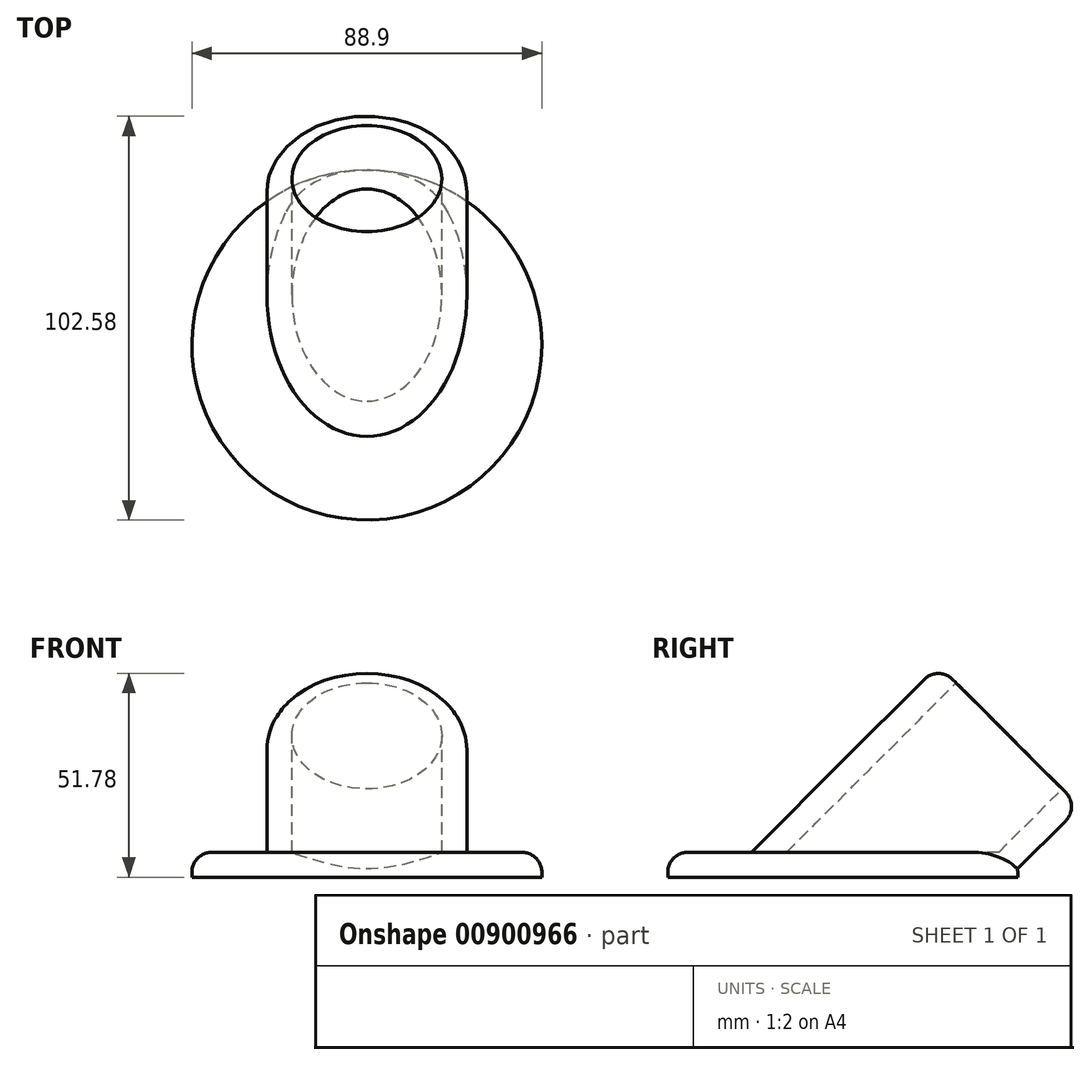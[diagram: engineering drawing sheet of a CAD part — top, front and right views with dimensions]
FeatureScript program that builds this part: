
annotation { "Feature Type Name" : "Feature", "Feature Type Description" : "" }
export const myFeature = defineFeature(function(context is Context, id is Id, definition is map)
    precondition{}
    {
        {
            var Q0;
            Q0=qCreatedBy(makeId("Top.planeOp"),FACE);
            var sketch = newSketch(context, id + "F0", { "sketchPlane" : qUnion([Q0])});
            skCircle(sketch, "E0", {"center": v(0, 0) * mm, "radius": 44.45 * mm});
            skSolve(sketch);
        }
        {
            var Q0;
            Q0=makeQuery(id+"F0.imprint","IMPRINT",FACE,{"disambiguationData":[TD([[makeQuery(id+"F0.imprint","IMPRINT",EDGE,{"derivedFrom":sQuery(id+"F0.wireOp",EDGE,"E0")}),1.0]])]});
            extrude(context, id + "F1", {"entities" : qUnion([Q0]), "depth" : 6.35 * mm, "offsetDistance" : 25.4 * mm});
        }
        {
            var Q0;
            Q0=qCreatedBy(makeId("Right.planeOp"),FACE);
            var sketch = newSketch(context, id + "F2", { "sketchPlane" : qUnion([Q0])});
            skLineSegment(sketch, "E1", {"start": v(0, 0) * mm, "end": v(0, 6.35) * mm});
            skLineSegment(sketch, "E2", {"start": v(0, 6.35) * mm, "end": v(35.92, 42.27) * mm});
            skSolve(sketch);
        }
        {
            var Q0;
            Q0=sQuery(id+"F2.wireOp",EDGE,"E2");
            var Q1;
            Q1=sQuery(id+"F2.wireOp",VERTEX,"E2.end");
            cPlane(context, id + "F3", {"entities" : qUnion([Q0, Q1]), "cplaneType" : CPlaneType.LINE_POINT, "offset" : 25.4 * mm, "width" : 152.4 * mm, "height" : 152.4 * mm});
        }
        {
            var Q0;
            Q0=qCreatedBy(id+"F3.planeOp",FACE);
            var sketch = newSketch(context, id + "F4", { "sketchPlane" : qUnion([Q0])});
            skPoint(sketch, "E3.0", {"position": v(0, -4.5) * mm});
            skCircle(sketch, "E4", {"center": v(0, -4.5) * mm, "radius": 19.05 * mm});
            skCircle(sketch, "E5", {"center": v(0, -4.5) * mm, "radius": 25.4 * mm});
            skSolve(sketch);
        }
        {
            var Q0;
            Q0=makeQuery(id+"F4.imprint","IMPRINT",FACE,{"disambiguationData":[TD([[makeQuery(id+"F4.imprint","IMPRINT",EDGE,{"derivedFrom":sQuery(id+"F4.wireOp",EDGE,"E4")}),-1.0]])]});
            var Q1;
            Q1=makeQuery(id+"F1.opExtrude","CAP_FACE",FACE,{"disambiguationData":[OSD([sQuery(id+"F0.wireOp",EDGE,"E0")])],"isStart":false});
            extrude(context, id + "F5", {"entities" : qUnion([Q0]), "operationType" : NewBodyOperationType.ADD, "endBound" : BoundingType.UP_TO_SURFACE, "oppositeDirection" : true, "depth" : 25.4 * mm, "endBoundEntityFace" : qUnion([Q1]), "offsetDistance" : 25.4 * mm});
        }
        {
            var Q0;
            Q0=makeQuery(id+"F5.opExtrude","CAP_EDGE",EDGE,{"disambiguationData":[OSD([sQuery(id+"F4.wireOp",EDGE,"E5")])],"isStart":false});
            fillet(context, id + "F6", {"entities" : qUnion([Q0]), "radius" : 12.7 * mm, "tangentPropagation" : true, "allowEdgeOverflow" : false});
        }
        {
            var Q0;
            Q0=makeQuery(id+"F1.opExtrude","CAP_EDGE",EDGE,{"disambiguationData":[OSD([sQuery(id+"F0.wireOp",EDGE,"E0")])],"isStart":false});
            fillet(context, id + "F7", {"entities" : qUnion([Q0]), "radius" : 5.08 * mm, "tangentPropagation" : true, "allowEdgeOverflow" : false});
        }
        {
            var Q0;
            Q0=makeQuery(id+"F5.opExtrude","CAP_EDGE",EDGE,{"disambiguationData":[OSD([sQuery(id+"F4.wireOp",EDGE,"E5")])],"isStart":true});
            fillet(context, id + "F8", {"entities" : qUnion([Q0]), "radius" : 5.08 * mm, "tangentPropagation" : true, "allowEdgeOverflow" : false});
        }
    });
